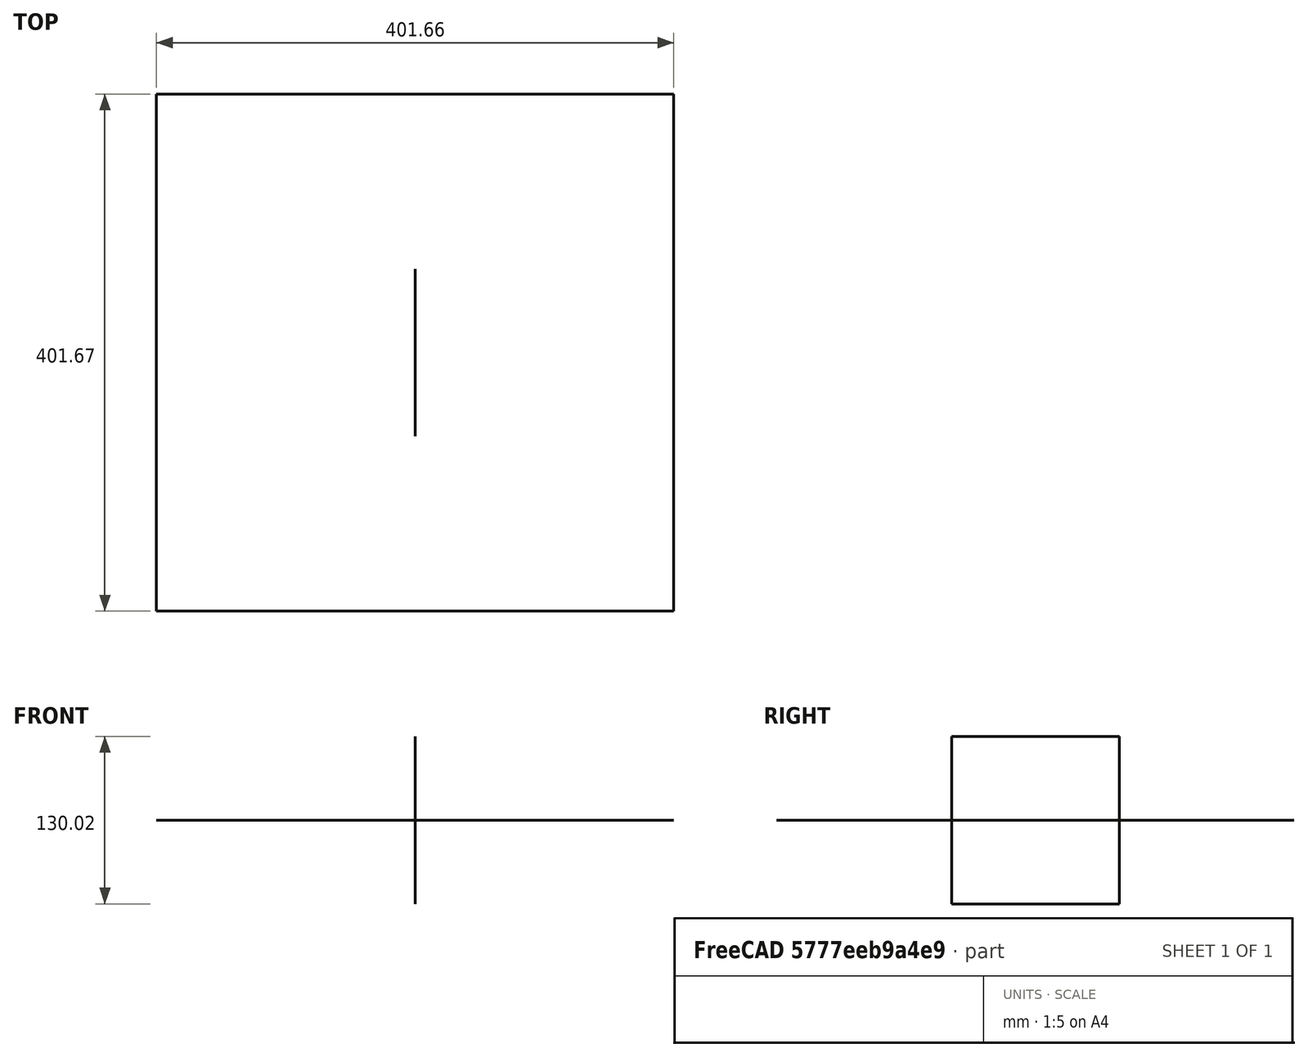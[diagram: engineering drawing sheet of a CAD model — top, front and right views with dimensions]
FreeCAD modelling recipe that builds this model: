
FCSTD DOCUMENT  (FreeCAD 2024.409R14555 (Git shallow))
Label: ValveGear_Z7S
License: All rights reserved
LicenseURL: https://en.wikipedia.org/wiki/All_rights_reserved
objects: Part::FeaturePython×97, App::FeaturePython×84, Sketcher::SketchObject×11, PartDesign::Body×11
note: 119 computed .brp shape members not serialized (recipe doc carries the construction recipe); baked Part::Feature solids carry a one-line shape summary decoded from their .brp

FEATURE [App::FeaturePython] Constraints  # WARN: FeaturePython — macro-defined, semantics opaque (R4)
  TreeRank = 13
  _LinkVersion = 1
  _Version = 1
FEATURE [Sketcher::SketchObject] Sketch001
  ArcFitTolerance = 1e-06
  AttachmentSupport = -> [XZ_Plane001]
  ExternalBSplineMaxDegree = 5
  ExternalBSplineTolerance = 0.0001
  FullyConstrained = true
  InternalTolerance = 1e-06
  InvalidShape = false
  MakeInternals = false
  MapMode = 5
  Placement = pos=(0,0,0) rot=(1,0,0;1.5708rad)
  Support = -> [XZ_Plane001]
  TreeRank = 29
  ValidateShape = false
  sketch-geometry (5):
    g0: Circle CenterX=0 CenterY=0 CenterZ=0 NormalX=0 NormalY=0 NormalZ=1 AngleXU=0 Radius=6.5
    g1: Circle CenterX=15 CenterY=0 CenterZ=0 NormalX=0 NormalY=0 NormalZ=1 AngleXU=0 Radius=3.5
    g2: LineSegment StartX=0 StartY=0 StartZ=0 EndX=15 EndY=0 EndZ=0
    g3: Circle CenterX=9e-16 CenterY=3.4 CenterZ=0 NormalX=0 NormalY=0 NormalZ=1 AngleXU=0 Radius=11
    g4: LineSegment StartX=9e-16 StartY=3.4 StartZ=0 EndX=0 EndY=0 EndZ=0
  constraints (12):
    c: Diameter(g0) = 13
    c: Coincident(g0,g-1)
    c: PointOnObject(g1,g-1)
    c: Diameter(g1) = 7
    c: Distance(g1,g0) = 15
    c: Coincident(g2,g0)
    c: Coincident(g2,g1)
    c: Diameter(g3) = 22
    c: Coincident(g4,g3)
    c: Coincident(g4,g0)
    c: Distance(g4) = 3.4
    c: Angle(g4,g2) = 4.71239
FEATURE [PartDesign::Body] Body001
  AutoGroupSolids = false
  ClaimAllChildren = false
  ExportMode = 0
  Group = -> [Sketch001]
  InvalidShape = false
  Origin = -> Origin001
  TreeRank = 28
  ValidateShape = false
  _ExportChildren = -> [Sketch001]
  _GroupVersion = 1
FEATURE [App::FeaturePython] Constraints001  # WARN: FeaturePython — macro-defined, semantics opaque (R4)
  TreeRank = 31
  _LinkVersion = 1
  _Version = 1
FEATURE [Part::FeaturePython] Parts001  # WARN: FeaturePython — macro-defined, semantics opaque (R4)
  Group = -> [Body001]
  GroupMode = 0
  InvalidShape = false
  TreeRank = 33
  ValidateShape = false
  _LinkVersion = 1
FEATURE [Sketcher::SketchObject] Sketch002
  ArcFitTolerance = 1e-06
  AttachmentSupport = -> [XZ_Plane002]
  ExternalBSplineMaxDegree = 5
  ExternalBSplineTolerance = 0.0001
  FullyConstrained = true
  InternalTolerance = 1e-06
  InvalidShape = false
  MakeInternals = false
  MapMode = 5
  Placement = pos=(0,0,0) rot=(1,0,0;1.5708rad)
  Support = -> [XZ_Plane002]
  TreeRank = 44
  ValidateShape = false
  sketch-geometry (3):
    g0: Circle CenterX=15 CenterY=0 CenterZ=0 NormalX=0 NormalY=0 NormalZ=1 AngleXU=0 Radius=4
    g1: LineSegment StartX=15 StartY=0 StartZ=0 EndX=-75 EndY=0 EndZ=0
    g2: Circle CenterX=-75 CenterY=0 CenterZ=0 NormalX=0 NormalY=0 NormalZ=1 AngleXU=0 Radius=3
  constraints (8):
    c: PointOnObject(g0,g-1)
    c: Distance(g-1,g0) = 15
    c: Diameter(g0) = 8
    c: Coincident(g1,g0)
    c: PointOnObject(g1,g-1)
    c: Distance(g1) = 90
    c: Coincident(g2,g1)
    c: Diameter(g2) = 6
FEATURE [PartDesign::Body] Body002
  AutoGroupSolids = false
  ClaimAllChildren = false
  ExportMode = 0
  Group = -> [Sketch002]
  InvalidShape = false
  Origin = -> Origin002
  TreeRank = 43
  ValidateShape = false
  _ExportChildren = -> [Sketch002]
  _GroupVersion = 1
FEATURE [App::FeaturePython] Constraints002  # WARN: FeaturePython — macro-defined, semantics opaque (R4)
  TreeRank = 46
  _LinkVersion = 1
  _Version = 1
FEATURE [Part::FeaturePython] Parts002  # WARN: FeaturePython — macro-defined, semantics opaque (R4)
  Group = -> [Body002]
  GroupMode = 0
  InvalidShape = false
  TreeRank = 48
  ValidateShape = false
  _LinkVersion = 1
FEATURE [Sketcher::SketchObject] Sketch003
  ArcFitTolerance = 1e-06
  AttachmentSupport = -> [XZ_Plane003]
  ExternalBSplineMaxDegree = 5
  ExternalBSplineTolerance = 0.0001
  FullyConstrained = false
  InternalTolerance = 1e-06
  InvalidShape = false
  MakeInternals = false
  MapMode = 5
  Placement = pos=(0,0,0) rot=(1,0,0;1.5708rad)
  Support = -> [XZ_Plane003]
  TreeRank = 68
  ValidateShape = false
  sketch-geometry (8):
    g0: Circle CenterX=-77.8195 CenterY=0 CenterZ=0 NormalX=0 NormalY=0 NormalZ=1 AngleXU=0 Radius=2
    g1: LineSegment StartX=-77.8195 StartY=0 StartZ=0 EndX=-133.569 EndY=0 EndZ=0
    g2: LineSegment StartX=-133.569 StartY=0 StartZ=0 EndX=-133.569 EndY=11 EndZ=0
    g3: LineSegment StartX=-133.569 StartY=11 StartZ=0 EndX=-143.069 EndY=11 EndZ=0
    g4: LineSegment StartX=-143.069 StartY=11 StartZ=0 EndX=-143.069 EndY=-11 EndZ=0
    g5: LineSegment StartX=-143.069 StartY=-11 StartZ=0 EndX=-133.569 EndY=-11 EndZ=0
    g6: LineSegment StartX=-133.569 StartY=-11 StartZ=0 EndX=-133.569 EndY=0 EndZ=0
    g7: GeomPoint [constr] X=-138.319 Y=0 Z=0
  constraints (20):
    c: PointOnObject(g0,g-1)
    c: Diameter(g0) = 4
    c: Coincident(g1,g0)
    c: Horizontal(g1)
    c: Distance(g1) = 55.75
    c: Coincident(g2,g1)
    c: Vertical(g2)
    c: Coincident(g3,g2)
    c: Horizontal(g3)
    c: Coincident(g4,g3)
    c: Vertical(g4)
    c: Coincident(g5,g4)
    c: Horizontal(g5)
    c: Coincident(g6,g5)
    c: Coincident(g6,g1)
    c: Distance(g4) = 22
    c: Symmetric(g2,g5,g1)
    c: Distance(g5) = 9.5
    c: PointOnObject(g7,g-1)
    c: Distance(g7,g1) = 4.75
FEATURE [PartDesign::Body] Body003
  AutoGroupSolids = false
  ClaimAllChildren = false
  ExportMode = 0
  Group = -> [Sketch003]
  InvalidShape = false
  Origin = -> Origin003
  TreeRank = 67
  ValidateShape = false
  _ExportChildren = -> [Sketch003]
  _GroupVersion = 1
FEATURE [App::FeaturePython] Constraints004  # WARN: FeaturePython — macro-defined, semantics opaque (R4)
  TreeRank = 70
  _LinkVersion = 1
  _Version = 1
FEATURE [Part::FeaturePython] Parts004  # WARN: FeaturePython — macro-defined, semantics opaque (R4)
  Group = -> [Body003]
  GroupMode = 0
  InvalidShape = false
  TreeRank = 72
  ValidateShape = false
  _LinkVersion = 1
FEATURE [Sketcher::SketchObject] Sketch004
  ArcFitTolerance = 1e-06
  AttachmentSupport = -> [XZ_Plane004]
  ExternalBSplineMaxDegree = 5
  ExternalBSplineTolerance = 0.0001
  FullyConstrained = false
  InternalTolerance = 1e-06
  InvalidShape = false
  MakeInternals = false
  MapMode = 5
  Placement = pos=(0,0,0) rot=(1,0,0;1.5708rad)
  Support = -> [XZ_Plane004]
  TreeRank = 136
  ValidateShape = false
  sketch-geometry (4):
    g0: LineSegment StartX=-73.0178 StartY=31.2839 StartZ=0 EndX=-54 EndY=-9.5 EndZ=0
    g1: Circle CenterX=-73.0178 CenterY=31.2839 CenterZ=0 NormalX=0 NormalY=0 NormalZ=1 AngleXU=0 Radius=45
    g2: LineSegment StartX=-54 StartY=-9.5 StartZ=0 EndX=-29 EndY=-9.5 EndZ=0
    g3: Circle CenterX=-54 CenterY=-9.5 CenterZ=0 NormalX=0 NormalY=0 NormalZ=1 AngleXU=0 Radius=1.13037
  constraints (10):
    c: Distance(g0) = 45
    c: Coincident(g1,g0)
    c: PointOnObject(g0,g1)
    c: Coincident(g2,g0)
    c: Horizontal(g2)
    c: Angle(g2,g0) = 2.00713  'Cutoff CTRL'
    c: Distance(g2) = 25
    c: DistanceX(g-2,g0) = -54
    c: DistanceY(g-1,g0) = -9.5
    c: Coincident(g3,g0)
FEATURE [PartDesign::Body] Body004
  AutoGroupSolids = false
  ClaimAllChildren = false
  ExportMode = 0
  Group = -> [Sketch004]
  InvalidShape = false
  Origin = -> Origin004
  TreeRank = 135
  ValidateShape = false
  _ExportChildren = -> [Sketch004]
  _GroupVersion = 1
FEATURE [App::FeaturePython] Constraints005  # WARN: FeaturePython — macro-defined, semantics opaque (R4)
  TreeRank = 138
  _LinkVersion = 1
  _Version = 1
FEATURE [Part::FeaturePython] Parts005  # WARN: FeaturePython — macro-defined, semantics opaque (R4)
  Group = -> [Body004]
  GroupMode = 0
  InvalidShape = false
  TreeRank = 140
  ValidateShape = false
  _LinkVersion = 1
FEATURE [Sketcher::SketchObject] Sketch005
  ArcFitTolerance = 1e-06
  AttachmentSupport = -> [XZ_Plane005]
  ExternalBSplineMaxDegree = 5
  ExternalBSplineTolerance = 0.0001
  FullyConstrained = false
  InternalTolerance = 1e-06
  InvalidShape = false
  MakeInternals = false
  MapMode = 5
  Placement = pos=(0,0,0) rot=(1,0,0;1.5708rad)
  Support = -> [XZ_Plane005]
  TreeRank = 152
  ValidateShape = false
  sketch-geometry (6):
    g0: LineSegment StartX=-16.5858 StartY=-34.3042 StartZ=0 EndX=-71.3858 EndY=-34.3042 EndZ=0
    g1: LineSegment StartX=-71.3858 StartY=-34.3042 StartZ=0 EndX=-91.3858 EndY=-34.3042 EndZ=0
    g2: LineSegment StartX=-71.3858 StartY=-34.3042 StartZ=0 EndX=-71.3858 EndY=-35.8042 EndZ=0
    g3: Circle CenterX=-16.5858 CenterY=-34.3042 CenterZ=0 NormalX=0 NormalY=0 NormalZ=1 AngleXU=0 Radius=11.25
    g4: Circle CenterX=-71.3858 CenterY=-35.8042 CenterZ=0 NormalX=0 NormalY=0 NormalZ=1 AngleXU=0 Radius=1
    g5: Circle CenterX=-91.3858 CenterY=-34.3042 CenterZ=0 NormalX=0 NormalY=0 NormalZ=1 AngleXU=0 Radius=1
  constraints (14):
    c: Horizontal(g0)
    c: Distance(g0) = 54.8
    c: Coincident(g1,g0)
    c: Horizontal(g1)
    c: Distance(g1) = 20
    c: Coincident(g2,g0)
    c: Vertical(g2)
    c: Distance(g2) = 1.5
    c: Coincident(g3,g0)
    c: Diameter(g3) = 22.5
    c: Coincident(g4,g2)
    c: Coincident(g5,g1)
    c: Diameter(g4) = 2
    c: Diameter(g5) = 2
FEATURE [PartDesign::Body] Body005
  AutoGroupSolids = false
  ClaimAllChildren = false
  ExportMode = 0
  Group = -> [Sketch005]
  InvalidShape = false
  Origin = -> Origin005
  TreeRank = 151
  ValidateShape = false
  _ExportChildren = -> [Sketch005]
  _GroupVersion = 1
FEATURE [App::FeaturePython] Constraints006  # WARN: FeaturePython — macro-defined, semantics opaque (R4)
  TreeRank = 154
  _LinkVersion = 1
  _Version = 1
FEATURE [Part::FeaturePython] Parts006  # WARN: FeaturePython — macro-defined, semantics opaque (R4)
  Group = -> [Body005]
  GroupMode = 0
  InvalidShape = false
  TreeRank = 156
  ValidateShape = false
  _LinkVersion = 1
FEATURE [Sketcher::SketchObject] Sketch006
  ArcFitTolerance = 1e-06
  AttachmentSupport = -> [XZ_Plane006]
  ExternalBSplineMaxDegree = 5
  ExternalBSplineTolerance = 0.0001
  FullyConstrained = false
  InternalTolerance = 1e-06
  InvalidShape = false
  MakeInternals = false
  MapMode = 5
  Placement = pos=(0,0,0) rot=(1,0,0;1.5708rad)
  Support = -> [XZ_Plane006]
  TreeRank = 195
  ValidateShape = false
  sketch-geometry (3):
    g0: LineSegment StartX=-79.4771 StartY=11.8151 StartZ=0 EndX=-79.4771 EndY=-10.4849 EndZ=0
    g1: Circle CenterX=-79.4771 CenterY=11.8151 CenterZ=0 NormalX=0 NormalY=0 NormalZ=1 AngleXU=0 Radius=2
    g2: Circle CenterX=-79.4771 CenterY=-10.4849 CenterZ=0 NormalX=0 NormalY=0 NormalZ=1 AngleXU=0 Radius=2
  constraints (6):
    c: Vertical(g0)
    c: Coincident(g1,g0)
    c: Coincident(g2,g0)
    c: Diameter(g1) = 4
    c: Equal(g1,g2)
    c: Distance(g0,g0) = 22.3
FEATURE [PartDesign::Body] Body006
  AutoGroupSolids = false
  ClaimAllChildren = false
  ExportMode = 0
  Group = -> [Sketch006]
  InvalidShape = false
  Origin = -> Origin006
  TreeRank = 194
  ValidateShape = false
  _ExportChildren = -> [Sketch006]
  _GroupVersion = 1
FEATURE [App::FeaturePython] Constraints007  # WARN: FeaturePython — macro-defined, semantics opaque (R4)
  TreeRank = 197
  _LinkVersion = 1
  _Version = 1
FEATURE [Part::FeaturePython] Parts007  # WARN: FeaturePython — macro-defined, semantics opaque (R4)
  Group = -> [Body006]
  GroupMode = 0
  InvalidShape = false
  TreeRank = 199
  ValidateShape = false
  _LinkVersion = 1
FEATURE [Sketcher::SketchObject] Sketch007
  ArcFitTolerance = 1e-06
  AttachmentSupport = -> [XZ_Plane007]
  ExternalBSplineMaxDegree = 5
  ExternalBSplineTolerance = 0.0001
  FullyConstrained = false
  InternalTolerance = 1e-06
  InvalidShape = false
  MakeInternals = false
  MapMode = 5
  Placement = pos=(0,0,0) rot=(1,0,0;1.5708rad)
  Support = -> [XZ_Plane007]
  TreeRank = 212
  ValidateShape = false
  sketch-geometry (5):
    g0: LineSegment StartX=-86.9461 StartY=28.8972 StartZ=0 EndX=-85.47 EndY=20.5263 EndZ=0
    g1: LineSegment StartX=-85.47 StartY=20.5263 StartZ=0 EndX=-76.97 EndY=20.5263 EndZ=0
    g2: Circle CenterX=-85.47 CenterY=20.5263 CenterZ=0 NormalX=0 NormalY=0 NormalZ=1 AngleXU=0 Radius=2
    g3: Circle CenterX=-76.97 CenterY=20.5263 CenterZ=0 NormalX=0 NormalY=0 NormalZ=1 AngleXU=0 Radius=1.5
    g4: Circle CenterX=-86.9461 CenterY=28.8972 CenterZ=0 NormalX=0 NormalY=0 NormalZ=1 AngleXU=0 Radius=1.5
  constraints (11):
    c: Coincident(g1,g0)
    c: Horizontal(g1)
    c: Distance(g0,g1) = 8.5
    c: Equal(g1,g0)
    c: Angle(g1,g0) = 1.74533
    c: Coincident(g2,g0)
    c: Coincident(g3,g1)
    c: Coincident(g4,g0)
    c: Diameter(g3) = 3
    c: Equal(g3,g4)
    c: Diameter(g2) = 4
FEATURE [PartDesign::Body] Body007
  AutoGroupSolids = false
  ClaimAllChildren = false
  ExportMode = 0
  Group = -> [Sketch007]
  InvalidShape = false
  Origin = -> Origin007
  TreeRank = 211
  ValidateShape = false
  _ExportChildren = -> [Sketch007]
  _GroupVersion = 1
FEATURE [App::FeaturePython] Constraints008  # WARN: FeaturePython — macro-defined, semantics opaque (R4)
  TreeRank = 214
  _LinkVersion = 1
  _Version = 1
FEATURE [Part::FeaturePython] Parts008  # WARN: FeaturePython — macro-defined, semantics opaque (R4)
  Group = -> [Body007]
  GroupMode = 0
  InvalidShape = false
  TreeRank = 216
  ValidateShape = false
  _LinkVersion = 1
FEATURE [Sketcher::SketchObject] Sketch008
  ArcFitTolerance = 1e-06
  AttachmentSupport = -> [XZ_Plane008]
  ExternalBSplineMaxDegree = 5
  ExternalBSplineTolerance = 0.0001
  FullyConstrained = false
  InternalTolerance = 1e-06
  InvalidShape = false
  MakeInternals = false
  MapMode = 5
  Placement = pos=(0,0,0) rot=(1,0,0;1.5708rad)
  Support = -> [XZ_Plane008]
  TreeRank = 246
  ValidateShape = false
  sketch-geometry (3):
    g0: LineSegment StartX=-86.6169 StartY=29.8279 StartZ=0 EndX=-98.6169 EndY=29.8279 EndZ=0
    g1: Circle CenterX=-86.6169 CenterY=29.8279 CenterZ=0 NormalX=0 NormalY=0 NormalZ=1 AngleXU=0 Radius=2
    g2: Circle CenterX=-98.6169 CenterY=29.8279 CenterZ=0 NormalX=0 NormalY=0 NormalZ=1 AngleXU=0 Radius=2
  constraints (6):
    c: Horizontal(g0)
    c: Distance(g0) = 12
    c: Coincident(g1,g0)
    c: Coincident(g2,g0)
    c: Diameter(g1) = 4
    c: Equal(g2,g1)
FEATURE [PartDesign::Body] Body008
  AutoGroupSolids = false
  ClaimAllChildren = false
  ExportMode = 0
  Group = -> [Sketch008]
  InvalidShape = false
  Origin = -> Origin008
  TreeRank = 245
  ValidateShape = false
  _ExportChildren = -> [Sketch008]
  _GroupVersion = 1
FEATURE [App::FeaturePython] Constraints009  # WARN: FeaturePython — macro-defined, semantics opaque (R4)
  TreeRank = 248
  _LinkVersion = 1
  _Version = 1
FEATURE [Part::FeaturePython] Parts009  # WARN: FeaturePython — macro-defined, semantics opaque (R4)
  Group = -> [Body008]
  GroupMode = 0
  InvalidShape = false
  TreeRank = 250
  ValidateShape = false
  _LinkVersion = 1
FEATURE [Sketcher::SketchObject] Sketch009
  ArcFitTolerance = 1e-06
  AttachmentSupport = -> [XZ_Plane009]
  ExternalBSplineMaxDegree = 5
  ExternalBSplineTolerance = 0.0001
  FullyConstrained = false
  InternalTolerance = 1e-06
  InvalidShape = false
  MakeInternals = false
  MapMode = 5
  Placement = pos=(0,0,0) rot=(1,0,0;1.5708rad)
  Support = -> [XZ_Plane009]
  TreeRank = 268
  ValidateShape = false
  sketch-geometry (13):
    g0: LineSegment StartX=-96.3044 StartY=29.3618 StartZ=0 EndX=-148.604 EndY=29.3618 EndZ=0
    g1: LineSegment StartX=-139.404 StartY=33.1118 StartZ=0 EndX=-139.404 EndY=25.6118 EndZ=0
    g2: LineSegment StartX=-139.404 StartY=33.1118 StartZ=0 EndX=-141.704 EndY=33.1118 EndZ=0
    g3: LineSegment StartX=-141.704 StartY=33.1118 StartZ=0 EndX=-141.704 EndY=25.6118 EndZ=0
    g4: LineSegment StartX=-141.704 StartY=25.6118 StartZ=0 EndX=-139.404 EndY=25.6118 EndZ=0
    g5: LineSegment StartX=-157.804 StartY=25.6118 StartZ=0 EndX=-157.804 EndY=33.1118 EndZ=0
    g6: LineSegment StartX=-157.804 StartY=33.1118 StartZ=0 EndX=-155.504 EndY=33.1118 EndZ=0
    g7: LineSegment StartX=-155.504 StartY=33.1118 StartZ=0 EndX=-155.504 EndY=25.6118 EndZ=0
    g8: LineSegment StartX=-155.504 StartY=25.6118 StartZ=0 EndX=-157.804 EndY=25.6118 EndZ=0
    g9: GeomPoint [constr] X=-156.654 Y=29.3618 Z=0
    g10: LineSegment StartX=-155.504 StartY=30.6118 StartZ=0 EndX=-141.704 EndY=30.6118 EndZ=0
    g11: LineSegment StartX=-155.504 StartY=28.1118 StartZ=0 EndX=-141.704 EndY=28.1118 EndZ=0
    g12: Circle CenterX=-96.3044 CenterY=29.3618 CenterZ=0 NormalX=0 NormalY=0 NormalZ=1 AngleXU=0 Radius=1.5
  constraints (35):
    c: Horizontal(g0)
    c: Distance(g0) = 52.3
    c: Distance(g1) = 7.5
    c: Symmetric(g1,g1,g0)
    c: Coincident(g2,g1)
    c: Horizontal(g2)
    c: Coincident(g3,g2)
    c: Vertical(g3)
    c: Coincident(g4,g3)
    c: Coincident(g4,g1)
    c: Horizontal(g4)
    c: Distance(g4) = 2.3
    c: Coincident(g5,g6)
    c: Coincident(g6,g7)
    c: Coincident(g7,g8)
    c: Coincident(g8,g5)
    c: Horizontal(g6)
    c: Horizontal(g8)
    c: Vertical(g5)
    c: Vertical(g7)
    c: Symmetric(g6,g5,g9)
    c: Horizontal(g9,g0)
    c: Equal(g6,g2)
    c: Equal(g5,g3)
    c: Distance(g5,g1) = 18.4
    c: Distance(g0,g1) = 9.2
    c: PointOnObject(g10,g7)
    c: PointOnObject(g10,g3)
    c: Horizontal(g10)
    c: PointOnObject(g11,g7)
    c: Horizontal(g11)
    c: Symmetric(g10,g11,g0)
    c: Distance(g10,g11) = 2.5
    c: Coincident(g12,g0)
    c: Diameter(g12) = 3
FEATURE [PartDesign::Body] Body009
  AutoGroupSolids = false
  ClaimAllChildren = false
  ExportMode = 0
  Group = -> [Sketch009]
  InvalidShape = false
  Origin = -> Origin009
  TreeRank = 267
  ValidateShape = false
  _ExportChildren = -> [Sketch009]
  _GroupVersion = 1
FEATURE [App::FeaturePython] Constraints010  # WARN: FeaturePython — macro-defined, semantics opaque (R4)
  TreeRank = 270
  _LinkVersion = 1
  _Version = 1
FEATURE [Part::FeaturePython] Parts010  # WARN: FeaturePython — macro-defined, semantics opaque (R4)
  Group = -> [Body009]
  GroupMode = 0
  InvalidShape = false
  TreeRank = 272
  ValidateShape = false
  _LinkVersion = 1
FEATURE [Sketcher::SketchObject] Sketch
  ArcFitTolerance = 1e-06
  AttachmentSupport = -> [XZ_Plane]
  ExternalBSplineMaxDegree = 5
  ExternalBSplineTolerance = 0.0001
  FullyConstrained = false
  InternalTolerance = 1e-06
  InvalidShape = false
  MakeInternals = false
  MapMode = 5
  Placement = pos=(0,0,0) rot=(1,0,0;1.5708rad)
  Support = -> [XZ_Plane]
  TreeRank = 315
  ValidateShape = false
  sketch-geometry (23):
    g0: LineSegment StartX=-180 StartY=63 StartZ=0 EndX=120 EndY=63 EndZ=0
    g1: LineSegment StartX=120 StartY=63 StartZ=0 EndX=120 EndY=-63 EndZ=0
    g2: LineSegment StartX=120 StartY=-63 StartZ=0 EndX=-180 EndY=-63 EndZ=0
    g3: LineSegment StartX=-180 StartY=-63 StartZ=0 EndX=-180 EndY=63 EndZ=0
    g4: Circle CenterX=0 CenterY=0 CenterZ=0 NormalX=0 NormalY=0 NormalZ=1 AngleXU=0 Radius=6.5
    g5: LineSegment StartX=0 StartY=0 StartZ=0 EndX=-180 EndY=0 EndZ=0
    g6: Circle CenterX=-54 CenterY=-9.5 CenterZ=0 NormalX=0 NormalY=0 NormalZ=1 AngleXU=0 Radius=1.5
    g7: Circle CenterX=-84 CenterY=11 CenterZ=0 NormalX=0 NormalY=0 NormalZ=1 AngleXU=0 Radius=1.27714
    g8: LineSegment StartX=-189.468 StartY=19 StartZ=0 EndX=0 EndY=19 EndZ=0
    g9: LineSegment StartX=-189.468 StartY=19 StartZ=0 EndX=-198.831 EndY=26.4354 EndZ=0
    g10: LineSegment StartX=-198.831 StartY=26.4354 StartZ=0 EndX=-198.831 EndY=11.5646 EndZ=0
    g11: LineSegment StartX=-198.831 StartY=11.5646 StartZ=0 EndX=-189.468 EndY=19 EndZ=0
    g12: LineSegment StartX=-180 StartY=0 StartZ=0 EndX=-192.162 EndY=6.36433 EndZ=0
    g13: LineSegment StartX=-192.162 StartY=6.36433 StartZ=0 EndX=-192.162 EndY=-6.36433 EndZ=0
    g14: LineSegment StartX=-192.162 StartY=-6.36433 StartZ=0 EndX=-180 EndY=0 EndZ=0
    g15: Circle CenterX=-150 CenterY=19 CenterZ=0 NormalX=0 NormalY=0 NormalZ=1 AngleXU=0 Radius=0.005
    g16: LineSegment StartX=0 StartY=0 StartZ=0 EndX=30 EndY=0 EndZ=0
    g17: LineSegment StartX=30 StartY=0 StartZ=0 EndX=34.0566 EndY=3.40069 EndZ=0
    g18: LineSegment StartX=34.0566 StartY=3.40069 StartZ=0 EndX=34.0566 EndY=-2.89461 EndZ=0
    g19: LineSegment StartX=34.0566 StartY=-2.89461 StartZ=0 EndX=30 EndY=-4e-16 EndZ=0
    g20: Circle CenterX=-150 CenterY=19 CenterZ=0 NormalX=0 NormalY=0 NormalZ=1 AngleXU=0 Radius=3.91179
    g21: LineSegment StartX=-150 StartY=63 StartZ=0 EndX=-150 EndY=-63 EndZ=0
    g22: LineSegment StartX=0 StartY=63 StartZ=0 EndX=0 EndY=-63 EndZ=0
  constraints (53):
    c: Coincident(g0,g1)
    c: Coincident(g1,g2)
    c: Coincident(g2,g3)
    c: Coincident(g3,g0)
    c: Horizontal(g0)
    c: Horizontal(g2)
    c: Vertical(g3)
    c: Distance(g1) = 126
    c: Symmetric(g0,g1,g-1)
    c: Distance(g-1,g3) = 180
    c: Coincident(g4,g-1)
    c: Diameter(g4) = 13
    c: Coincident(g5,g4)
    c: PointOnObject(g5,g3)
    c: Horizontal(g5)
    c: Diameter(g6) = 3
    c: Distance(g6,g5) = 9.5
    c: DistanceX(g-2,g6) = -54
    c: DistanceX(g7,g6) = 30
    c: DistanceY(g4,g7) = 11
    c: Horizontal(g8)
    c: Coincident(g9,g8)
    c: Coincident(g11,g10)
    c: Coincident(g11,g8)
    c: Coincident(g10,g9)
    c: DistanceY(g4,g8) = 19
    c: Coincident(g12,g5)
    c: Coincident(g13,g12)
    c: Coincident(g14,g13)
    c: Coincident(g14,g5)
    c: Symmetric(g13,g12,g5)
    c: Symmetric(g10,g9,g8)
    c: Diameter(g15) = 0.01
    c: DistanceX(g-2,g15) = -150
    c: Distance(g15,g5) = 19
    c: Coincident(g16,g4)
    c: PointOnObject(g16,g-1)
    c: Coincident(g17,g16)
    c: Coincident(g18,g17)
    c: Vertical(g18)
    c: Coincident(g19,g18)
    c: Coincident(g19,g16)
    c: Distance(g4,g16) = 30  'Dead Centre'
    c: Coincident(g20,g15)
    c: PointOnObject(g21,g0)
    c: PointOnObject(g21,g2)
    c: Vertical(g21)
    c: Distance(g4,g21) = 150
    c: PointOnObject(g22,g0)
    c: PointOnObject(g22,g2)
    c: Vertical(g22)
    c: Vertical(g22,g4)
    c: Vertical(g8,g4)
FEATURE [PartDesign::Body] Body
  AutoGroupSolids = false
  ClaimAllChildren = false
  ExportMode = 0
  Group = -> [Sketch]
  InvalidShape = false
  Origin = -> Origin
  TreeRank = 10
  ValidateShape = false
  _ExportChildren = -> [Sketch]
  _GroupVersion = 1
FEATURE [Part::FeaturePython] Parts  # WARN: FeaturePython — macro-defined, semantics opaque (R4)
  Group = -> [Body]
  GroupMode = 0
  InvalidShape = false
  TreeRank = 15
  ValidateShape = false
  _LinkVersion = 1
FEATURE [Sketcher::SketchObject] Sketch010
  ArcFitTolerance = 1e-06
  AttachmentSupport = -> [XZ_Plane010]
  ExternalBSplineMaxDegree = 5
  ExternalBSplineTolerance = 0.0001
  FullyConstrained = false
  InternalTolerance = 1e-06
  InvalidShape = false
  MakeInternals = false
  MapMode = 5
  Placement = pos=(0,0,0) rot=(1,0,0;1.5708rad)
  Support = -> [XZ_Plane010]
  TreeRank = 337
  ValidateShape = false
  sketch-geometry (15):
    g0: LineSegment StartX=-128 StartY=-12.0827 StartZ=0 EndX=-150 EndY=-12.0827 EndZ=0
    g1: LineSegment StartX=-150 StartY=-12.0827 StartZ=0 EndX=-172 EndY=-12.0827 EndZ=0
    g2: LineSegment StartX=-172 StartY=-12.0827 StartZ=0 EndX=-172 EndY=14.9774 EndZ=0
    g3: LineSegment StartX=-158 StartY=14.9774 StartZ=0 EndX=-150 EndY=14.9774 EndZ=0
    g4: LineSegment StartX=-150 StartY=14.9774 StartZ=0 EndX=-142 EndY=14.9774 EndZ=0
    g5: LineSegment StartX=-159.5 StartY=14.9774 StartZ=0 EndX=-172 EndY=14.9774 EndZ=0
    g6: LineSegment StartX=-128 StartY=-12.0827 StartZ=0 EndX=-128 EndY=14.9774 EndZ=0
    g7: LineSegment StartX=-128 StartY=14.9774 StartZ=0 EndX=-140.5 EndY=14.9774 EndZ=0
    g8: LineSegment StartX=-164.568 StartY=11.4567 StartZ=0 EndX=-150 EndY=11.4567 EndZ=0
    g9: LineSegment StartX=-150 StartY=11.4567 StartZ=0 EndX=-135.432 EndY=11.4567 EndZ=0
    g10: LineSegment StartX=-158 StartY=14.9774 StartZ=0 EndX=-164.568 EndY=11.4567 EndZ=0
    g11: LineSegment StartX=-142 StartY=14.9774 StartZ=0 EndX=-135.432 EndY=11.4567 EndZ=0
    g12: LineSegment StartX=-159.5 StartY=14.9774 StartZ=0 EndX=-172 EndY=11.6516 EndZ=0
    g13: LineSegment StartX=-140.5 StartY=14.9774 StartZ=0 EndX=-128 EndY=11.6516 EndZ=0
    g14: GeomPoint [constr] X=0 Y=0 Z=0
  constraints (36):
    c: Horizontal(g0)
    c: DistanceX(g-2,g0) = -150
    c: Coincident(g1,g0)
    c: Symmetric(g1,g0,g0)
    c: Distance(g0,g0) = 22
    c: Coincident(g2,g1)
    c: Vertical(g2)
    c: Horizontal(g3)
    c: Coincident(g4,g3)
    c: Symmetric(g4,g3,g3)
    c: Vertical(g3,g0)
    c: Distance(g3,g4) = 8
    c: Horizontal(g5)
    c: Horizontal(g5,g3)
    c: Distance(g5,g3) = 1.5
    c: Coincident(g2,g5)
    c: Coincident(g6,g0)
    c: Vertical(g6)
    c: Equal(g6,g2)
    c: Coincident(g7,g6)
    c: Horizontal(g7)
    c: Equal(g7,g5)
    c: Horizontal(g8)
    c: Vertical(g8,g3)
    c: Coincident(g9,g8)
    c: Symmetric(g9,g8,g8)
    c: Coincident(g10,g3)
    c: Coincident(g10,g8)
    c: Coincident(g11,g4)
    c: Coincident(g11,g9)
    c: Coincident(g12,g5)
    c: PointOnObject(g12,g2)
    c: Coincident(g13,g7)
    c: PointOnObject(g13,g6)
    c: Equal(g12,g13)
    c: Coincident(g14,g-1)
FEATURE [PartDesign::Body] Body010
  AutoGroupSolids = false
  ClaimAllChildren = false
  ExportMode = 0
  Group = -> [Sketch010]
  InvalidShape = false
  Origin = -> Origin010
  TreeRank = 336
  ValidateShape = false
  _ExportChildren = -> [Sketch010]
  _GroupVersion = 1
FEATURE [Part::FeaturePython] Assembly  # WARN: FeaturePython — macro-defined, semantics opaque (R4)
  AutoRelax = true
  BuildShape = 0
  Freeze = false
  Group = -> [Constraints,Elements,Parts]
  InvalidShape = false
  Placement = pos=(-4.26503e-11,0.00833303,-5.51265e-07) rot=(-1,0,0;0.000132rad)
  TreeRank = 12
  ValidateShape = false
  Verbose = false
  _LinkVersion = 1
  _SolverType = 1
  _Version = 1
FEATURE [App::FeaturePython] Elements  # WARN: FeaturePython — macro-defined, semantics opaque (R4)
  Group = -> [_Element,Element007,Element008,Element009,Element015,Element021,Element026,Element028,Element029,Element031,Element033,Element035,Element036]
  TreeRank = 14
  _LinkVersion = 1
FEATURE [Part::FeaturePython] _Element  # link proxy (typed FeaturePython)
  Detach = false
  InvalidShape = false
  LinkTransform = true
  LinkedObject = -> Body [Sketch.Edge5]
  TreeRank = 18
  ValidateShape = false
  _LinkVersion = 1
  _Parent = -> Elements
FEATURE [Part::FeaturePython] Assembly001  # WARN: FeaturePython — macro-defined, semantics opaque (R4)
  AutoRelax = true
  BuildShape = 0
  Freeze = false
  Group = -> [Constraints001,Elements001,Parts001]
  InvalidShape = false
  Placement = pos=(-4.27174e-11,0.00833336,-5.51309e-07) rot=(1,0,0;6.28305rad)
  TreeRank = 30
  ValidateShape = false
  Verbose = false
  _LinkVersion = 1
  _SolverType = 1
  _Version = 1
FEATURE [App::FeaturePython] Elements001  # WARN: FeaturePython — macro-defined, semantics opaque (R4)
  Group = -> [Element,Element001,Element002,Element027]
  TreeRank = 32
  _LinkVersion = 1
FEATURE [Part::FeaturePython] Assembly002  # WARN: FeaturePython — macro-defined, semantics opaque (R4)
  AutoRelax = true
  BuildShape = 0
  Freeze = false
  Group = -> [Constraints002,Elements002,Parts002]
  InvalidShape = false
  Placement = pos=(1.58905e-10,0.00833336,-5.51309e-07) rot=(-1,0,0;0.000132rad)
  TreeRank = 45
  ValidateShape = false
  Verbose = false
  _LinkVersion = 1
  _SolverType = 1
  _Version = 1
FEATURE [App::FeaturePython] Elements002  # WARN: FeaturePython — macro-defined, semantics opaque (R4)
  Group = -> [Element003,Element004]
  TreeRank = 47
  _LinkVersion = 1
FEATURE [Part::FeaturePython] Assembly003  # WARN: FeaturePython — macro-defined, semantics opaque (R4)
  AutoRelax = true
  BuildShape = 0
  Freeze = false
  Group = -> [Constraints003,Elements003,Parts003]
  InvalidShape = false
  TreeRank = 49
  ValidateShape = false
  Verbose = false
  _LinkVersion = 1
  _SolverType = 1
  _Version = 1
FEATURE [App::FeaturePython] Constraints003  # WARN: FeaturePython — macro-defined, semantics opaque (R4)
  Group = -> [Constraint,Constraint001,Constraint002,Constraint003,Constraint004,Constraint005,Constraint007,Constraint008,Constraint009,Constraint010,Constraint011,Constraint012,Constraint013,Constraint014,Constraint015,Constraint016,Constraint018,Constraint019,Constraint020,Constraint021,Constraint022]
  TreeRank = 50
  _LinkVersion = 1
  _Version = 1
FEATURE [App::FeaturePython] Elements003  # WARN: FeaturePython — macro-defined, semantics opaque (R4)
  Group = -> [_Element001,_Element002,_Element003,_Element004,_Element005,_Element006,_Element007,_Element008,_Element009,_Element011,_Element012,_Element013,_Element014,_Element015,_Element016,_Element017,_Element018,_Element019,_Element020,_Element021,_Element022,_Element023,_Element024,_Element025,_Element026,_Element028,_Element029,_Element030,_Element031,_Element032,_Element033,_Element034,_Element035,+4 more]
  TreeRank = 51
  _LinkVersion = 1
FEATURE [Part::FeaturePython] Parts003  # WARN: FeaturePython — macro-defined, semantics opaque (R4)
  Group = -> [Assembly002,Assembly001,Assembly,Assembly004,Assembly005,Assembly006,Assembly007,Assembly008,Assembly009,Assembly010]
  GroupMode = 0
  InvalidShape = false
  TreeRank = 52
  ValidateShape = false
  _LinkVersion = 1
FEATURE [Part::FeaturePython] Element  # link proxy (typed FeaturePython)
  Detach = false
  InvalidShape = false
  LinkTransform = true
  LinkedObject = -> Body001 [Sketch001.Edge1]
  TreeRank = 53
  ValidateShape = false
  _LinkVersion = 1
  _Parent = -> Elements001
FEATURE [Part::FeaturePython] Element001  # link proxy (typed FeaturePython)
  Detach = false
  InvalidShape = false
  LinkTransform = true
  LinkedObject = -> Body001 [Sketch001.Edge5]
  TreeRank = 54
  ValidateShape = false
  _LinkVersion = 1
  _Parent = -> Elements001
FEATURE [Part::FeaturePython] Element002  # link proxy (typed FeaturePython)
  Detach = false
  InvalidShape = false
  LinkTransform = true
  LinkedObject = -> Body001 [Sketch001.Edge2]
  TreeRank = 55
  ValidateShape = false
  _LinkVersion = 1
  _Parent = -> Elements001
FEATURE [Part::FeaturePython] Element003  # link proxy (typed FeaturePython)
  Detach = false
  InvalidShape = false
  LinkTransform = true
  LinkedObject = -> Body002 [Sketch002.Edge1]
  TreeRank = 56
  ValidateShape = false
  _LinkVersion = 1
  _Parent = -> Elements002
FEATURE [Part::FeaturePython] Element004  # link proxy (typed FeaturePython)
  Detach = false
  InvalidShape = false
  LinkTransform = true
  LinkedObject = -> Body002 [Sketch002.Edge3]
  TreeRank = 57
  ValidateShape = false
  _LinkVersion = 1
  _Parent = -> Elements002
FEATURE [Part::FeaturePython] Assembly004  # WARN: FeaturePython — macro-defined, semantics opaque (R4)
  AutoRelax = true
  BuildShape = 0
  Freeze = false
  Group = -> [Constraints004,Elements004,Parts004]
  InvalidShape = false
  Placement = pos=(2.81946,0.00833091,-0.0185483) rot=(-0.485257,0.874371,-5.8e-05;0.000273rad)
  TreeRank = 69
  ValidateShape = false
  Verbose = false
  _LinkVersion = 1
  _SolverType = 1
  _Version = 1
FEATURE [App::FeaturePython] Elements004  # WARN: FeaturePython — macro-defined, semantics opaque (R4)
  Group = -> [Element005,Element006,Element030]
  TreeRank = 71
  _LinkVersion = 1
FEATURE [Part::FeaturePython] Element005  # link proxy (typed FeaturePython)
  Detach = false
  InvalidShape = false
  LinkTransform = true
  LinkedObject = -> Body003 [Sketch003.Edge1]
  TreeRank = 73
  ValidateShape = false
  _LinkVersion = 1
  _Parent = -> Elements004
FEATURE [Part::FeaturePython] Element006  # link proxy (typed FeaturePython)
  Detach = false
  InvalidShape = false
  LinkTransform = true
  LinkedObject = -> Body003 [Sketch003.Edge2]
  TreeRank = 74
  ValidateShape = false
  _LinkVersion = 1
  _Parent = -> Elements004
FEATURE [App::FeaturePython] Constraint  label="Locked"  # WARN: FeaturePython — macro-defined, semantics opaque (R4)
  Disabled = false
  Group = -> [ElementLink]
  TreeRank = 75
  _ConstraintType = 0
  _LinkVersion = 1
  _Parent = -> Constraints003
FEATURE [App::FeaturePython] ElementLink  label="_Element001"  # link proxy (typed FeaturePython)
  LinkTransform = true
  LinkedObject = -> _Element001
  TreeRank = 76
  _LinkVersion = 1
  _Parent = -> Constraint
FEATURE [Part::FeaturePython] Element007  # link proxy (typed FeaturePython)
  Detach = false
  InvalidShape = false
  LinkTransform = true
  LinkedObject = -> Body [Sketch.Edge3]
  TreeRank = 77
  ValidateShape = false
  _LinkVersion = 1
  _Parent = -> Elements
FEATURE [Part::FeaturePython] _Element001  # link proxy (typed FeaturePython)
  Detach = false
  InvalidShape = false
  LinkTransform = true
  LinkedObject = -> Assembly [1.$Element007.]
  TreeRank = 78
  ValidateShape = false
  _LinkVersion = 1
  _Parent = -> Elements003
FEATURE [Part::FeaturePython] _Element002  # link proxy (typed FeaturePython)
  Detach = false
  InvalidShape = false
  LinkTransform = true
  LinkedObject = -> Assembly [1.$_Element.]
  TreeRank = 81
  ValidateShape = false
  _LinkVersion = 1
  _Parent = -> Elements003
FEATURE [Part::FeaturePython] _Element003  # link proxy (typed FeaturePython)
  Detach = false
  InvalidShape = false
  LinkTransform = true
  LinkedObject = -> Assembly001 [1.$Element.]
  TreeRank = 83
  ValidateShape = false
  _LinkVersion = 1
  _Parent = -> Elements003
FEATURE [App::FeaturePython] Constraint001  label="PlaneCoincident.Driver"  # WARN: FeaturePython — macro-defined, semantics opaque (R4)
  Angle = 360
  AnglePitch = 0
  AngleRoll = 0
  Cascade = false
  Disabled = false
  Group = -> [ElementLink001,ElementLink002]
  LockAngle = true
  Multiply = false
  OffsetX = 0
  OffsetY = 0
  TreeRank = 84
  _ConstraintType = 35
  _LinkVersion = 1
  _Parent = -> Constraints003
FEATURE [App::FeaturePython] ElementLink001  label="_Element002"  # link proxy (typed FeaturePython)
  LinkTransform = true
  LinkedObject = -> _Element002
  TreeRank = 85
  _LinkVersion = 1
  _Parent = -> Constraint001
FEATURE [App::FeaturePython] ElementLink002  label="_Element003"  # link proxy (typed FeaturePython)
  LinkTransform = true
  LinkedObject = -> _Element003
  TreeRank = 86
  _LinkVersion = 1
  _Parent = -> Constraint001
FEATURE [App::FeaturePython] Constraint002  label="PlaneCoincident001"  # WARN: FeaturePython — macro-defined, semantics opaque (R4)
  Angle = 0
  AnglePitch = 0
  AngleRoll = 0
  Cascade = false
  Disabled = false
  Group = -> [ElementLink003,ElementLink004]
  LockAngle = false
  Multiply = false
  OffsetX = 0
  OffsetY = 0
  TreeRank = 87
  _ConstraintType = 35
  _LinkVersion = 1
  _Parent = -> Constraints003
FEATURE [App::FeaturePython] ElementLink003  label="_Element004"  # link proxy (typed FeaturePython)
  LinkTransform = true
  LinkedObject = -> _Element004
  TreeRank = 88
  _LinkVersion = 1
  _Parent = -> Constraint002
FEATURE [Part::FeaturePython] _Element004  # link proxy (typed FeaturePython)
  Detach = false
  InvalidShape = false
  LinkTransform = true
  LinkedObject = -> Assembly001 [1.$Element002.]
  TreeRank = 89
  ValidateShape = false
  _LinkVersion = 1
  _Parent = -> Elements003
FEATURE [App::FeaturePython] ElementLink004  label="_Element005"  # link proxy (typed FeaturePython)
  LinkTransform = true
  LinkedObject = -> _Element005
  TreeRank = 90
  _LinkVersion = 1
  _Parent = -> Constraint002
FEATURE [Part::FeaturePython] _Element005  # link proxy (typed FeaturePython)
  Detach = false
  InvalidShape = false
  LinkTransform = true
  LinkedObject = -> Assembly002 [1.$Element003.]
  TreeRank = 91
  ValidateShape = false
  _LinkVersion = 1
  _Parent = -> Elements003
FEATURE [App::FeaturePython] Constraint003  label="PlaneCoincident002"  # WARN: FeaturePython — macro-defined, semantics opaque (R4)
  Angle = 0
  AnglePitch = 0
  AngleRoll = 0
  Cascade = false
  Disabled = false
  Group = -> [ElementLink005,ElementLink006]
  LockAngle = false
  Multiply = false
  OffsetX = 0
  OffsetY = 0
  TreeRank = 92
  _ConstraintType = 35
  _LinkVersion = 1
  _Parent = -> Constraints003
FEATURE [App::FeaturePython] ElementLink005  label="_Element006"  # link proxy (typed FeaturePython)
  LinkTransform = true
  LinkedObject = -> _Element006
  TreeRank = 93
  _LinkVersion = 1
  _Parent = -> Constraint003
FEATURE [Part::FeaturePython] _Element006  # link proxy (typed FeaturePython)
  Detach = false
  InvalidShape = false
  LinkTransform = true
  LinkedObject = -> Assembly002 [1.$Element004.]
  TreeRank = 94
  ValidateShape = false
  _LinkVersion = 1
  _Parent = -> Elements003
FEATURE [App::FeaturePython] ElementLink006  label="_Element007"  # link proxy (typed FeaturePython)
  LinkTransform = true
  LinkedObject = -> _Element007
  TreeRank = 95
  _LinkVersion = 1
  _Parent = -> Constraint003
FEATURE [Part::FeaturePython] _Element007  # link proxy (typed FeaturePython)
  Detach = false
  InvalidShape = false
  LinkTransform = true
  LinkedObject = -> Assembly004 [1.$Element005.]
  TreeRank = 96
  ValidateShape = false
  _LinkVersion = 1
  _Parent = -> Elements003
FEATURE [Part::FeaturePython] Element008  # link proxy (typed FeaturePython)
  Detach = false
  InvalidShape = false
  LinkTransform = true
  LinkedObject = -> Body [Sketch.edge6]
  TreeRank = 97
  ValidateShape = false
  _LinkVersion = 1
  _Parent = -> Elements
FEATURE [Part::FeaturePython] _Element008  # link proxy (typed FeaturePython)
  Detach = false
  InvalidShape = false
  LinkTransform = true
  LinkedObject = -> Assembly [1.$Element008.]
  TreeRank = 100
  ValidateShape = false
  _LinkVersion = 1
  _Parent = -> Elements003
FEATURE [Part::FeaturePython] _Element009  # link proxy (typed FeaturePython)
  Detach = false
  InvalidShape = false
  LinkTransform = true
  LinkedObject = -> Assembly004 [1.$Element006.]
  TreeRank = 102
  ValidateShape = false
  _LinkVersion = 1
  _Parent = -> Elements003
FEATURE [Part::FeaturePython] Element009  # link proxy (typed FeaturePython)
  Detach = false
  InvalidShape = false
  LinkTransform = true
  LinkedObject = -> Body [Sketch.Edge14]
  TreeRank = 114
  ValidateShape = false
  _LinkVersion = 1
  _Parent = -> Elements
FEATURE [Part::FeaturePython] _Element011  # link proxy (typed FeaturePython)
  Detach = false
  InvalidShape = false
  LinkTransform = true
  LinkedObject = -> Assembly [1.$Element009.]
  TreeRank = 125
  ValidateShape = false
  _LinkVersion = 1
  _Parent = -> Elements003
FEATURE [Part::FeaturePython] Assembly005  # WARN: FeaturePython — macro-defined, semantics opaque (R4)
  AutoRelax = true
  BuildShape = 0
  Freeze = false
  Group = -> [Constraints005,Elements005,Parts005]
  InvalidShape = false
  Placement = pos=(-4.28482e-11,0.00833303,-5.51265e-07) rot=(-1,0,0;0.000132rad)
  TreeRank = 137
  ValidateShape = false
  Verbose = false
  _LinkVersion = 1
  _SolverType = 1
  _Version = 1
FEATURE [App::FeaturePython] Elements005  # WARN: FeaturePython — macro-defined, semantics opaque (R4)
  Group = -> [Element010,Element014]
  TreeRank = 139
  _LinkVersion = 1
FEATURE [Part::FeaturePython] Element010  # link proxy (typed FeaturePython)
  Detach = false
  InvalidShape = false
  LinkTransform = true
  LinkedObject = -> Body004 [Sketch004.Edge3]
  TreeRank = 141
  ValidateShape = false
  _LinkVersion = 1
  _Parent = -> Elements005
FEATURE [Part::FeaturePython] Assembly006  # WARN: FeaturePython — macro-defined, semantics opaque (R4)
  AutoRelax = true
  BuildShape = 0
  Freeze = false
  Group = -> [Constraints006,Elements006,Parts006]
  InvalidShape = false
  Placement = pos=(9.27701,0.0136716,40.3568) rot=(-0.000645,-1,6.6e-05;0.204413rad)
  TreeRank = 153
  ValidateShape = false
  Verbose = false
  _LinkVersion = 1
  _SolverType = 1
  _Version = 1
FEATURE [App::FeaturePython] Elements006  # WARN: FeaturePython — macro-defined, semantics opaque (R4)
  Group = -> [Element011,Element012,Element013]
  TreeRank = 155
  _LinkVersion = 1
FEATURE [Part::FeaturePython] Element011  # link proxy (typed FeaturePython)
  Detach = false
  InvalidShape = false
  LinkTransform = true
  LinkedObject = -> Body005 [Sketch005.Edge4]
  TreeRank = 157
  ValidateShape = false
  _LinkVersion = 1
  _Parent = -> Elements006
FEATURE [Part::FeaturePython] Element012  # link proxy (typed FeaturePython)
  Detach = false
  InvalidShape = false
  LinkTransform = true
  LinkedObject = -> Body005 [Sketch005.Edge5]
  TreeRank = 158
  ValidateShape = false
  _LinkVersion = 1
  _Parent = -> Elements006
FEATURE [Part::FeaturePython] Element013  # link proxy (typed FeaturePython)
  Detach = false
  InvalidShape = false
  LinkTransform = true
  LinkedObject = -> Body005 [Sketch005.Edge6]
  TreeRank = 159
  ValidateShape = false
  _LinkVersion = 1
  _Parent = -> Elements006
FEATURE [App::FeaturePython] Constraint005  label="PlaneCoincident003"  # WARN: FeaturePython — macro-defined, semantics opaque (R4)
  Angle = 0
  AnglePitch = 0
  AngleRoll = 0
  Cascade = false
  Disabled = false
  Group = -> [ElementLink009,ElementLink010]
  LockAngle = false
  Multiply = false
  OffsetX = 0
  OffsetY = 0
  TreeRank = 160
  _ConstraintType = 35
  _LinkVersion = 1
  _Parent = -> Constraints003
FEATURE [App::FeaturePython] ElementLink009  label="_Element012"  # link proxy (typed FeaturePython)
  LinkTransform = true
  LinkedObject = -> _Element012
  TreeRank = 161
  _LinkVersion = 1
  _Parent = -> Constraint005
FEATURE [Part::FeaturePython] _Element012  # link proxy (typed FeaturePython)
  Detach = false
  InvalidShape = false
  LinkTransform = true
  LinkedObject = -> Assembly001 [1.$Element001.]
  TreeRank = 162
  ValidateShape = false
  _LinkVersion = 1
  _Parent = -> Elements003
FEATURE [App::FeaturePython] ElementLink010  label="_Element013"  # link proxy (typed FeaturePython)
  LinkTransform = true
  LinkedObject = -> _Element013
  TreeRank = 163
  _LinkVersion = 1
  _Parent = -> Constraint005
FEATURE [Part::FeaturePython] _Element013  # link proxy (typed FeaturePython)
  Detach = false
  InvalidShape = false
  LinkTransform = true
  LinkedObject = -> Assembly006 [1.$Element011.]
  TreeRank = 164
  ValidateShape = false
  _LinkVersion = 1
  _Parent = -> Elements003
FEATURE [Part::FeaturePython] _Element014  # link proxy (typed FeaturePython)
  Detach = false
  InvalidShape = false
  LinkTransform = true
  LinkedObject = -> Assembly006 [1.$Element012.]
  TreeRank = 167
  ValidateShape = false
  _LinkVersion = 1
  _Parent = -> Elements003
FEATURE [Part::FeaturePython] _Element015  # link proxy (typed FeaturePython)
  Detach = false
  InvalidShape = false
  LinkTransform = true
  LinkedObject = -> Assembly005 [1.$Element010.]
  TreeRank = 169
  ValidateShape = false
  _LinkVersion = 1
  _Parent = -> Elements003
FEATURE [Part::FeaturePython] Element014  # link proxy (typed FeaturePython)
  Detach = false
  InvalidShape = false
  LinkTransform = true
  LinkedObject = -> Body004 [Sketch004.Edge4]
  TreeRank = 170
  ValidateShape = false
  _LinkVersion = 1
  _Parent = -> Elements005
FEATURE [App::FeaturePython] Constraint007  label="PlaneCoincident004"  # WARN: FeaturePython — macro-defined, semantics opaque (R4)
  Angle = 0
  AnglePitch = 0
  AngleRoll = 0
  Cascade = false
  Disabled = false
  Group = -> [ElementLink013,ElementLink014]
  LockAngle = true
  Multiply = false
  OffsetX = 0
  OffsetY = 0
  TreeRank = 171
  _ConstraintType = 35
  _LinkVersion = 1
  _Parent = -> Constraints003
FEATURE [App::FeaturePython] ElementLink013  label="_Element011"  # link proxy (typed FeaturePython)
  LinkTransform = true
  LinkedObject = -> _Element011
  TreeRank = 172
  _LinkVersion = 1
  _Parent = -> Constraint007
FEATURE [App::FeaturePython] ElementLink014  label="_Element016"  # link proxy (typed FeaturePython)
  LinkTransform = true
  LinkedObject = -> _Element016
  TreeRank = 173
  _LinkVersion = 1
  _Parent = -> Constraint007
FEATURE [Part::FeaturePython] _Element016  # link proxy (typed FeaturePython)
  Detach = false
  InvalidShape = false
  LinkTransform = true
  LinkedObject = -> Assembly005 [1.$Element014.]
  TreeRank = 174
  ValidateShape = false
  _LinkVersion = 1
  _Parent = -> Elements003
FEATURE [App::FeaturePython] Constraint008  label="PointsOnCircle001"  # WARN: FeaturePython — macro-defined, semantics opaque (R4)
  Disabled = false
  Group = -> [ElementLink015,ElementLink016]
  TreeRank = 175
  _ConstraintType = 26
  _LinkVersion = 1
  _Parent = -> Constraints003
FEATURE [App::FeaturePython] ElementLink015  label="_Element014"  # link proxy (typed FeaturePython)
  LinkTransform = true
  LinkedObject = -> _Element014
  TreeRank = 176
  _LinkVersion = 1
  _Parent = -> Constraint008
FEATURE [App::FeaturePython] ElementLink016  label="_Element015"  # link proxy (typed FeaturePython)
  LinkTransform = true
  LinkedObject = -> _Element015
  TreeRank = 177
  _LinkVersion = 1
  _Parent = -> Constraint008
FEATURE [App::FeaturePython] Constraint009  label="PointOnLine"  # WARN: FeaturePython — macro-defined, semantics opaque (R4)
  Disabled = false
  Group = -> [ElementLink017,ElementLink018]
  TreeRank = 178
  _ConstraintType = 4
  _LinkVersion = 1
  _Parent = -> Constraints003
FEATURE [App::FeaturePython] ElementLink017  label="_Element007"  # link proxy (typed FeaturePython)
  LinkTransform = true
  LinkedObject = -> _Element007
  TreeRank = 179
  _LinkVersion = 1
  _Parent = -> Constraint009
FEATURE [App::FeaturePython] ElementLink018  label="_Element008"  # link proxy (typed FeaturePython)
  LinkTransform = true
  LinkedObject = -> _Element008
  TreeRank = 180
  _LinkVersion = 1
  _Parent = -> Constraint009
FEATURE [App::FeaturePython] ElementLink007  label="_Element008"  # link proxy (typed FeaturePython)
  LinkTransform = true
  LinkedObject = -> _Element008
  TreeRank = 181
  _LinkVersion = 1
  _Parent = -> Constraint004
FEATURE [App::FeaturePython] ElementLink008  label="_Element009"  # link proxy (typed FeaturePython)
  LinkTransform = true
  LinkedObject = -> _Element009
  TreeRank = 182
  _LinkVersion = 1
  _Parent = -> Constraint004
FEATURE [App::FeaturePython] Constraint004  label="MultiParallel"  # WARN: FeaturePython — macro-defined, semantics opaque (R4)
  Angle = 0
  AnglePitch = 0
  AngleRoll = 0
  Disabled = true
  Group = -> [ElementLink007,ElementLink008]
  LockAngle = false
  TreeRank = 183
  _ConstraintType = 291
  _LinkVersion = 1
  _Parent = -> Constraints003
FEATURE [Part::FeaturePython] Element015  # link proxy (typed FeaturePython)
  Detach = false
  InvalidShape = false
  LinkTransform = true
  LinkedObject = -> Body [Sketch.edge8]
  TreeRank = 184
  ValidateShape = false
  _LinkVersion = 1
  _Parent = -> Elements
FEATURE [Part::FeaturePython] Assembly007  # WARN: FeaturePython — macro-defined, semantics opaque (R4)
  AutoRelax = true
  BuildShape = 0
  Freeze = false
  Group = -> [Constraints007,Elements007,Parts007]
  InvalidShape = false
  Placement = pos=(4.74708,0.00922847,6.76695) rot=(-0.001291,-0.999999,6.6e-05;0.102356rad)
  TreeRank = 196
  ValidateShape = false
  Verbose = false
  _LinkVersion = 1
  _SolverType = 1
  _Version = 1
FEATURE [App::FeaturePython] Elements007  # WARN: FeaturePython — macro-defined, semantics opaque (R4)
  Group = -> [Element016,Element017,Element034]
  TreeRank = 198
  _LinkVersion = 1
FEATURE [Part::FeaturePython] Element016  # link proxy (typed FeaturePython)
  Detach = false
  InvalidShape = false
  LinkTransform = true
  LinkedObject = -> Body006 [Sketch006.Edge3]
  TreeRank = 200
  ValidateShape = false
  _LinkVersion = 1
  _Parent = -> Elements007
FEATURE [Part::FeaturePython] Element017  # link proxy (typed FeaturePython)
  Detach = false
  InvalidShape = false
  LinkTransform = true
  LinkedObject = -> Body006 [Sketch006.Edge2]
  TreeRank = 201
  ValidateShape = false
  _LinkVersion = 1
  _Parent = -> Elements007
FEATURE [Part::FeaturePython] Assembly008  # WARN: FeaturePython — macro-defined, semantics opaque (R4)
  AutoRelax = true
  BuildShape = 0
  Freeze = false
  Group = -> [Constraints008,Elements008,Parts008]
  InvalidShape = false
  Placement = pos=(-0.193868,0.00628124,-15.514) rot=(-0.00187,0.999998,-6.6e-05;0.070715rad)
  TreeRank = 213
  ValidateShape = false
  Verbose = false
  _LinkVersion = 1
  _SolverType = 1
  _Version = 1
FEATURE [App::FeaturePython] Elements008  # WARN: FeaturePython — macro-defined, semantics opaque (R4)
  Group = -> [Element018,Element019,Element020]
  TreeRank = 215
  _LinkVersion = 1
FEATURE [Part::FeaturePython] Element018  # link proxy (typed FeaturePython)
  Detach = false
  InvalidShape = false
  LinkTransform = true
  LinkedObject = -> Body007 [Sketch007.Edge3]
  TreeRank = 217
  ValidateShape = false
  _LinkVersion = 1
  _Parent = -> Elements008
FEATURE [Part::FeaturePython] Element019  # link proxy (typed FeaturePython)
  Detach = false
  InvalidShape = false
  LinkTransform = true
  LinkedObject = -> Body007 [Sketch007.Edge4]
  TreeRank = 218
  ValidateShape = false
  _LinkVersion = 1
  _Parent = -> Elements008
FEATURE [Part::FeaturePython] Element020  # link proxy (typed FeaturePython)
  Detach = false
  InvalidShape = false
  LinkTransform = true
  LinkedObject = -> Body007 [Sketch007.Edge5]
  TreeRank = 219
  ValidateShape = false
  _LinkVersion = 1
  _Parent = -> Elements008
FEATURE [App::FeaturePython] Constraint010  label="PlaneCoincident"  # WARN: FeaturePython — macro-defined, semantics opaque (R4)
  Angle = 0
  AnglePitch = 0
  AngleRoll = 0
  Cascade = false
  Disabled = false
  Group = -> [ElementLink019,ElementLink020]
  LockAngle = false
  Multiply = false
  OffsetX = 0
  OffsetY = 0
  TreeRank = 220
  _ConstraintType = 35
  _LinkVersion = 1
  _Parent = -> Constraints003
FEATURE [App::FeaturePython] ElementLink019  label="_Element017"  # link proxy (typed FeaturePython)
  LinkTransform = true
  LinkedObject = -> _Element017
  TreeRank = 221
  _LinkVersion = 1
  _Parent = -> Constraint010
FEATURE [Part::FeaturePython] _Element017  # link proxy (typed FeaturePython)
  Detach = false
  InvalidShape = false
  LinkTransform = true
  LinkedObject = -> Assembly007 [1.$Element016.]
  TreeRank = 222
  ValidateShape = false
  _LinkVersion = 1
  _Parent = -> Elements003
FEATURE [App::FeaturePython] ElementLink020  label="_Element018"  # link proxy (typed FeaturePython)
  LinkTransform = true
  LinkedObject = -> _Element018
  TreeRank = 223
  _LinkVersion = 1
  _Parent = -> Constraint010
FEATURE [Part::FeaturePython] _Element018  # link proxy (typed FeaturePython)
  Detach = false
  InvalidShape = false
  LinkTransform = true
  LinkedObject = -> Assembly006 [1.$Element013.]
  TreeRank = 224
  ValidateShape = false
  _LinkVersion = 1
  _Parent = -> Elements003
FEATURE [App::FeaturePython] Constraint011  label="PlaneCoincident005"  # WARN: FeaturePython — macro-defined, semantics opaque (R4)
  Angle = 0
  AnglePitch = 0
  AngleRoll = 0
  Cascade = false
  Disabled = false
  Group = -> [ElementLink021,ElementLink022]
  LockAngle = false
  Multiply = false
  OffsetX = 0
  OffsetY = 0
  TreeRank = 225
  _ConstraintType = 35
  _LinkVersion = 1
  _Parent = -> Constraints003
FEATURE [App::FeaturePython] ElementLink021  label="_Element019"  # link proxy (typed FeaturePython)
  LinkTransform = true
  LinkedObject = -> _Element019
  TreeRank = 226
  _LinkVersion = 1
  _Parent = -> Constraint011
FEATURE [Part::FeaturePython] _Element019  # link proxy (typed FeaturePython)
  Detach = false
  InvalidShape = false
  LinkTransform = true
  LinkedObject = -> Assembly008 [1.$Element018.]
  TreeRank = 227
  ValidateShape = false
  _LinkVersion = 1
  _Parent = -> Elements003
FEATURE [App::FeaturePython] ElementLink022  label="_Element020"  # link proxy (typed FeaturePython)
  LinkTransform = true
  LinkedObject = -> _Element020
  TreeRank = 228
  _LinkVersion = 1
  _Parent = -> Constraint011
FEATURE [Part::FeaturePython] _Element020  # link proxy (typed FeaturePython)
  Detach = false
  InvalidShape = false
  LinkTransform = true
  LinkedObject = -> Assembly [1.$Element015.]
  TreeRank = 229
  ValidateShape = false
  _LinkVersion = 1
  _Parent = -> Elements003
FEATURE [App::FeaturePython] Constraint012  label="PlaneCoincident006"  # WARN: FeaturePython — macro-defined, semantics opaque (R4)
  Angle = 0
  AnglePitch = 0
  AngleRoll = 0
  Cascade = false
  Disabled = false
  Group = -> [ElementLink023,ElementLink024]
  LockAngle = false
  Multiply = false
  OffsetX = 0
  OffsetY = 0
  TreeRank = 230
  _ConstraintType = 35
  _LinkVersion = 1
  _Parent = -> Constraints003
FEATURE [App::FeaturePython] ElementLink023  label="_Element021"  # link proxy (typed FeaturePython)
  LinkTransform = true
  LinkedObject = -> _Element021
  TreeRank = 231
  _LinkVersion = 1
  _Parent = -> Constraint012
FEATURE [Part::FeaturePython] _Element021  # link proxy (typed FeaturePython)
  Detach = false
  InvalidShape = false
  LinkTransform = true
  LinkedObject = -> Assembly008 [1.$Element019.]
  TreeRank = 232
  ValidateShape = false
  _LinkVersion = 1
  _Parent = -> Elements003
FEATURE [App::FeaturePython] ElementLink024  label="_Element022"  # link proxy (typed FeaturePython)
  LinkTransform = true
  LinkedObject = -> _Element022
  TreeRank = 233
  _LinkVersion = 1
  _Parent = -> Constraint012
FEATURE [Part::FeaturePython] _Element022  # link proxy (typed FeaturePython)
  Detach = false
  InvalidShape = false
  LinkTransform = true
  LinkedObject = -> Assembly007 [1.$Element017.]
  TreeRank = 234
  ValidateShape = false
  _LinkVersion = 1
  _Parent = -> Elements003
FEATURE [Part::FeaturePython] Element021  # link proxy (typed FeaturePython)
  Detach = false
  InvalidShape = false
  LinkTransform = true
  LinkedObject = -> Body [Sketch.Edge19]
  TreeRank = 235
  ValidateShape = false
  _LinkVersion = 1
  _Parent = -> Elements
FEATURE [Part::FeaturePython] Assembly009  # WARN: FeaturePython — macro-defined, semantics opaque (R4)
  AutoRelax = true
  BuildShape = 0
  Freeze = false
  Group = -> [Constraints009,Elements009,Parts009]
  InvalidShape = false
  Placement = pos=(2.80302,0.0073977,-7.07357) rot=(-0.003493,-0.999994,6.6e-05;0.037862rad)
  TreeRank = 247
  ValidateShape = false
  Verbose = false
  _LinkVersion = 1
  _SolverType = 1
  _Version = 1
FEATURE [App::FeaturePython] Elements009  # WARN: FeaturePython — macro-defined, semantics opaque (R4)
  Group = -> [Element022,Element023]
  TreeRank = 249
  _LinkVersion = 1
FEATURE [Part::FeaturePython] Element022  # link proxy (typed FeaturePython)
  Detach = false
  InvalidShape = false
  LinkTransform = true
  LinkedObject = -> Body008 [Sketch008.Edge3]
  TreeRank = 251
  ValidateShape = false
  _LinkVersion = 1
  _Parent = -> Elements009
FEATURE [Part::FeaturePython] Element023  # link proxy (typed FeaturePython)
  Detach = false
  InvalidShape = false
  LinkTransform = true
  LinkedObject = -> Body008 [Sketch008.Edge2]
  TreeRank = 252
  ValidateShape = false
  _LinkVersion = 1
  _Parent = -> Elements009
FEATURE [App::FeaturePython] Constraint013  label="PlaneCoincident007"  # WARN: FeaturePython — macro-defined, semantics opaque (R4)
  Angle = 0
  AnglePitch = 0
  AngleRoll = 0
  Cascade = false
  Disabled = false
  Group = -> [ElementLink025,ElementLink026]
  LockAngle = false
  Multiply = false
  OffsetX = 0
  OffsetY = 0
  TreeRank = 253
  _ConstraintType = 35
  _LinkVersion = 1
  _Parent = -> Constraints003
FEATURE [App::FeaturePython] ElementLink025  label="_Element023"  # link proxy (typed FeaturePython)
  LinkTransform = true
  LinkedObject = -> _Element023
  TreeRank = 254
  _LinkVersion = 1
  _Parent = -> Constraint013
FEATURE [Part::FeaturePython] _Element023  # link proxy (typed FeaturePython)
  Detach = false
  InvalidShape = false
  LinkTransform = true
  LinkedObject = -> Assembly009 [1.$Element023.]
  TreeRank = 255
  ValidateShape = false
  _LinkVersion = 1
  _Parent = -> Elements003
FEATURE [App::FeaturePython] ElementLink026  label="_Element024"  # link proxy (typed FeaturePython)
  LinkTransform = true
  LinkedObject = -> _Element024
  TreeRank = 256
  _LinkVersion = 1
  _Parent = -> Constraint013
FEATURE [Part::FeaturePython] _Element024  # link proxy (typed FeaturePython)
  Detach = false
  InvalidShape = false
  LinkTransform = true
  LinkedObject = -> Assembly008 [1.$Element020.]
  TreeRank = 257
  ValidateShape = false
  _LinkVersion = 1
  _Parent = -> Elements003
FEATURE [Part::FeaturePython] Assembly010  # WARN: FeaturePython — macro-defined, semantics opaque (R4)
  AutoRelax = true
  BuildShape = 0
  Freeze = false
  Group = -> [Constraints010,Elements010,Parts010]
  InvalidShape = false
  Placement = pos=(-0.567846,0.00696275,-10.3618) rot=(-1,0,0;0.000132rad)
  TreeRank = 269
  ValidateShape = false
  Verbose = false
  _LinkVersion = 1
  _SolverType = 1
  _Version = 1
FEATURE [App::FeaturePython] Elements010  # WARN: FeaturePython — macro-defined, semantics opaque (R4)
  Group = -> [Element024,Element025,Element032]
  TreeRank = 271
  _LinkVersion = 1
FEATURE [Part::FeaturePython] Element024  # link proxy (typed FeaturePython)
  Detach = false
  InvalidShape = false
  LinkTransform = true
  LinkedObject = -> Body009 [Sketch009.Edge12]
  TreeRank = 273
  ValidateShape = false
  _LinkVersion = 1
  _Parent = -> Elements010
FEATURE [App::FeaturePython] Constraint014  label="PlaneCoincident008"  # WARN: FeaturePython — macro-defined, semantics opaque (R4)
  Angle = 0
  AnglePitch = 0
  AngleRoll = 0
  Cascade = false
  Disabled = false
  Group = -> [ElementLink027,ElementLink028]
  LockAngle = false
  Multiply = false
  OffsetX = 0
  OffsetY = 0
  TreeRank = 275
  _ConstraintType = 35
  _LinkVersion = 1
  _Parent = -> Constraints003
FEATURE [App::FeaturePython] ElementLink027  label="_Element025"  # link proxy (typed FeaturePython)
  LinkTransform = true
  LinkedObject = -> _Element025
  TreeRank = 276
  _LinkVersion = 1
  _Parent = -> Constraint014
FEATURE [Part::FeaturePython] _Element025  # link proxy (typed FeaturePython)
  Detach = false
  InvalidShape = false
  LinkTransform = true
  LinkedObject = -> Assembly010 [1.$Element024.]
  TreeRank = 277
  ValidateShape = false
  _LinkVersion = 1
  _Parent = -> Elements003
FEATURE [App::FeaturePython] ElementLink028  label="_Element026"  # link proxy (typed FeaturePython)
  LinkTransform = true
  LinkedObject = -> _Element026
  TreeRank = 278
  _LinkVersion = 1
  _Parent = -> Constraint014
FEATURE [Part::FeaturePython] _Element026  # link proxy (typed FeaturePython)
  Detach = false
  InvalidShape = false
  LinkTransform = true
  LinkedObject = -> Assembly009 [1.$Element022.]
  TreeRank = 279
  ValidateShape = false
  _LinkVersion = 1
  _Parent = -> Elements003
FEATURE [Part::FeaturePython] _Element028  # link proxy (typed FeaturePython)
  Detach = false
  InvalidShape = false
  LinkTransform = true
  LinkedObject = -> Assembly [1.$Element021.]
  TreeRank = 284
  ValidateShape = false
  _LinkVersion = 1
  _Parent = -> Elements003
FEATURE [App::FeaturePython] Constraint015  label="PointOnLine001"  # WARN: FeaturePython — macro-defined, semantics opaque (R4)
  Disabled = false
  Group = -> [ElementLink029,ElementLink030]
  TreeRank = 285
  _ConstraintType = 4
  _LinkVersion = 1
  _Parent = -> Constraints003
FEATURE [App::FeaturePython] ElementLink029  label="_Element025"  # link proxy (typed FeaturePython)
  LinkTransform = true
  LinkedObject = -> _Element025
  TreeRank = 286
  _LinkVersion = 1
  _Parent = -> Constraint015
FEATURE [App::FeaturePython] ElementLink030  label="_Element028"  # link proxy (typed FeaturePython)
  LinkTransform = true
  LinkedObject = -> _Element028
  TreeRank = 287
  _LinkVersion = 1
  _Parent = -> Constraint015
FEATURE [Part::FeaturePython] Element025  # link proxy (typed FeaturePython)
  Detach = false
  InvalidShape = false
  LinkTransform = true
  LinkedObject = -> Body009 [Sketch009.Vertex2]
  TreeRank = 288
  ValidateShape = false
  _LinkVersion = 1
  _Parent = -> Elements010
FEATURE [App::FeaturePython] Constraint016  label="PointOnLine002"  # WARN: FeaturePython — macro-defined, semantics opaque (R4)
  Disabled = false
  Group = -> [ElementLink031,ElementLink032]
  TreeRank = 289
  _ConstraintType = 4
  _LinkVersion = 1
  _Parent = -> Constraints003
FEATURE [App::FeaturePython] ElementLink031  label="_Element029"  # link proxy (typed FeaturePython)
  LinkTransform = true
  LinkedObject = -> _Element029
  TreeRank = 290
  _LinkVersion = 1
  _Parent = -> Constraint016
FEATURE [Part::FeaturePython] _Element029  # link proxy (typed FeaturePython)
  Detach = false
  InvalidShape = false
  LinkTransform = true
  LinkedObject = -> Assembly010 [1.$Element025.]
  TreeRank = 291
  ValidateShape = false
  _LinkVersion = 1
  _Parent = -> Elements003
FEATURE [App::FeaturePython] ElementLink032  label="_Element028"  # link proxy (typed FeaturePython)
  LinkTransform = true
  LinkedObject = -> _Element028
  TreeRank = 292
  _LinkVersion = 1
  _Parent = -> Constraint016
FEATURE [Part::FeaturePython] Element026  # link proxy (typed FeaturePython)
  Detach = false
  InvalidShape = false
  LinkTransform = true
  LinkedObject = -> Body [Sketch.Edge20]
  TreeRank = 293
  ValidateShape = false
  _LinkVersion = 1
  _Parent = -> Elements
FEATURE [Part::FeaturePython] _Element030  # link proxy (typed FeaturePython)
  Detach = false
  InvalidShape = false
  LinkTransform = true
  LinkedObject = -> Assembly [1.$Element026.]
  TreeRank = 297
  ValidateShape = false
  _LinkVersion = 1
  _Parent = -> Elements003
FEATURE [Part::FeaturePython] Element027  # link proxy (typed FeaturePython)
  Detach = false
  InvalidShape = false
  LinkTransform = true
  LinkedObject = -> Body001 [Sketch001.Edge4]
  TreeRank = 298
  ValidateShape = false
  _LinkVersion = 1
  _Parent = -> Elements001
FEATURE [Part::FeaturePython] Element028  # link proxy (typed FeaturePython)
  Detach = false
  InvalidShape = false
  LinkTransform = true
  LinkedObject = -> Body [Sketch.Edge9]
  TreeRank = 299
  ValidateShape = false
  _LinkVersion = 1
  _Parent = -> Elements
FEATURE [App::FeaturePython] Constraint018  label="MeasureAngle"  # WARN: FeaturePython — macro-defined, semantics opaque (R4)
  Angle = 0
  Disabled = false
  Group = -> [ElementLink035,ElementLink036]
  Supplement = false
  TreeRank = 300
  _ConstraintType = 43
  _LinkVersion = 1
  _Parent = -> Constraints003
  expr: Label2 = .Angle
FEATURE [App::FeaturePython] ElementLink035  label="_Element031"  # link proxy (typed FeaturePython)
  LinkTransform = true
  LinkedObject = -> _Element031
  TreeRank = 301
  _LinkVersion = 1
  _Parent = -> Constraint018
FEATURE [Part::FeaturePython] _Element031  # link proxy (typed FeaturePython)
  Detach = false
  InvalidShape = false
  LinkTransform = true
  LinkedObject = -> Assembly001 [1.$Element027.]
  TreeRank = 302
  ValidateShape = false
  _LinkVersion = 1
  _Parent = -> Elements003
FEATURE [App::FeaturePython] ElementLink036  label="_Element032"  # link proxy (typed FeaturePython)
  LinkTransform = true
  LinkedObject = -> _Element032
  TreeRank = 303
  _LinkVersion = 1
  _Parent = -> Constraint018
FEATURE [Part::FeaturePython] _Element032  # link proxy (typed FeaturePython)
  Detach = false
  InvalidShape = false
  LinkTransform = true
  LinkedObject = -> Assembly [1.$Element028.]
  TreeRank = 304
  ValidateShape = false
  _LinkVersion = 1
  _Parent = -> Elements003
FEATURE [Part::FeaturePython] Element029  # link proxy (typed FeaturePython)
  Detach = false
  InvalidShape = false
  LinkTransform = true
  LinkedObject = -> Body [Sketch.Edge4]
  TreeRank = 305
  ValidateShape = false
  _LinkVersion = 1
  _Parent = -> Elements
FEATURE [Part::FeaturePython] Element030  # link proxy (typed FeaturePython)
  Detach = false
  InvalidShape = false
  LinkTransform = true
  LinkedObject = -> Body003 [Sketch003.vertex14]
  TreeRank = 306
  ValidateShape = false
  _LinkVersion = 1
  _Parent = -> Elements004
FEATURE [App::FeaturePython] Constraint019  label="MeasurePointLine"  # WARN: FeaturePython — macro-defined, semantics opaque (R4)
  Disabled = false
  Distance = 44.5
  Group = -> [ElementLink037,ElementLink038]
  TreeRank = 307
  _ConstraintType = 41
  _LinkVersion = 1
  _Parent = -> Constraints003
  expr: Label2 = .Distance
FEATURE [App::FeaturePython] ElementLink037  label="_Element033"  # link proxy (typed FeaturePython)
  LinkTransform = true
  LinkedObject = -> _Element033
  TreeRank = 308
  _LinkVersion = 1
  _Parent = -> Constraint019
FEATURE [Part::FeaturePython] _Element033  # link proxy (typed FeaturePython)
  Detach = false
  InvalidShape = false
  LinkTransform = true
  LinkedObject = -> Assembly004 [1.$Element030.]
  TreeRank = 309
  ValidateShape = false
  _LinkVersion = 1
  _Parent = -> Elements003
FEATURE [App::FeaturePython] ElementLink038  label="_Element034"  # link proxy (typed FeaturePython)
  LinkTransform = true
  LinkedObject = -> _Element034
  TreeRank = 310
  _LinkVersion = 1
  _Parent = -> Constraint019
FEATURE [Part::FeaturePython] _Element034  # link proxy (typed FeaturePython)
  Detach = false
  InvalidShape = false
  LinkTransform = true
  LinkedObject = -> Assembly [1.$Element029.]
  TreeRank = 311
  ValidateShape = false
  _LinkVersion = 1
  _Parent = -> Elements003
FEATURE [Part::FeaturePython] Element031  # link proxy (typed FeaturePython)
  Detach = false
  InvalidShape = false
  LinkTransform = true
  LinkedObject = -> Body [Sketch.Edge23]
  TreeRank = 316
  ValidateShape = false
  _LinkVersion = 1
  _Parent = -> Elements
FEATURE [Part::FeaturePython] Element032  # link proxy (typed FeaturePython)
  Detach = false
  InvalidShape = false
  LinkTransform = true
  LinkedObject = -> Body009 [Sketch009.Edge2]
  TreeRank = 317
  ValidateShape = false
  _LinkVersion = 1
  _Parent = -> Elements010
FEATURE [Part::FeaturePython] _Element035  # link proxy (typed FeaturePython)
  Detach = false
  InvalidShape = false
  LinkTransform = true
  LinkedObject = -> Assembly [1.$Element031.]
  TreeRank = 321
  ValidateShape = false
  _LinkVersion = 1
  _Parent = -> Elements003
FEATURE [Part::FeaturePython] Element033  # link proxy (typed FeaturePython)
  Detach = false
  InvalidShape = false
  LinkTransform = true
  LinkedObject = -> Body [Sketch.vertex15]
  TreeRank = 322
  ValidateShape = false
  _LinkVersion = 1
  _Parent = -> Elements
FEATURE [App::FeaturePython] Constraint020  label="MeasurePoints"  # WARN: FeaturePython — macro-defined, semantics opaque (R4)
  Disabled = false
  Distance = 149.172
  Group = -> [ElementLink039,ElementLink040]
  TreeRank = 323
  _ConstraintType = 40
  _LinkVersion = 1
  _Parent = -> Constraints003
  expr: Label2 = .Distance
FEATURE [App::FeaturePython] ElementLink039  label="_Element029"  # link proxy (typed FeaturePython)
  LinkTransform = true
  LinkedObject = -> _Element029
  TreeRank = 324
  _LinkVersion = 1
  _Parent = -> Constraint020
FEATURE [App::FeaturePython] ElementLink040  label="_Element036"  # link proxy (typed FeaturePython)
  LinkTransform = true
  LinkedObject = -> _Element036
  TreeRank = 325
  _LinkVersion = 1
  _Parent = -> Constraint020
FEATURE [Part::FeaturePython] _Element036  # link proxy (typed FeaturePython)
  Detach = false
  InvalidShape = false
  LinkTransform = true
  LinkedObject = -> Assembly [1.$Element033.]
  TreeRank = 326
  ValidateShape = false
  _LinkVersion = 1
  _Parent = -> Elements003
FEATURE [Part::FeaturePython] Element034  # link proxy (typed FeaturePython)
  Detach = false
  InvalidShape = false
  LinkTransform = true
  LinkedObject = -> Body006 [Sketch006.Vertex2]
  TreeRank = 340
  ValidateShape = false
  _LinkVersion = 1
  _Parent = -> Elements007
FEATURE [Part::FeaturePython] _Element037  # link proxy (typed FeaturePython)
  Detach = false
  InvalidShape = false
  LinkTransform = true
  LinkedObject = -> Assembly007 [1.$Element034.]
  TreeRank = 341
  ValidateShape = false
  _LinkVersion = 1
  _Parent = -> Elements003
FEATURE [Part::FeaturePython] Element035  label="YZ-plane@Body@"  # link proxy (typed FeaturePython)
  Detach = false
  InvalidShape = false
  LinkTransform = true
  LinkedObject = -> Body [Origin.YZ_Plane.]
  TreeRank = 343
  ValidateShape = false
  _LinkVersion = 1
  _Parent = -> Elements
FEATURE [Part::FeaturePython] _Element038  label="YZ-plane@Assembly@"  # link proxy (typed FeaturePython)
  Detach = false
  InvalidShape = false
  LinkTransform = true
  LinkedObject = -> Assembly [1.$YZ-plane@Body@.]
  TreeRank = 344
  ValidateShape = false
  _LinkVersion = 1
  _Parent = -> Elements003
FEATURE [App::FeaturePython] Constraint021  label="MeasurePointPlane"  # WARN: FeaturePython — macro-defined, semantics opaque (R4)
  Disabled = false
  Distance = -73.2427
  Group = -> [ElementLink041,ElementLink042]
  TreeRank = 345
  _ConstraintType = 42
  _LinkVersion = 1
  _Parent = -> Constraints003
  expr: Label2 = .Distance
FEATURE [App::FeaturePython] ElementLink041  label="_Element037"  # link proxy (typed FeaturePython)
  LinkTransform = true
  LinkedObject = -> _Element037
  TreeRank = 346
  _LinkVersion = 1
  _Parent = -> Constraint021
FEATURE [App::FeaturePython] ElementLink042  label="YZ-plane@Assembly@"  # link proxy (typed FeaturePython)
  LinkTransform = true
  LinkedObject = -> _Element038
  TreeRank = 347
  _LinkVersion = 1
  _Parent = -> Constraint021
FEATURE [App::FeaturePython] Constraint022  label="MeasurePointPlane001"  # WARN: FeaturePython — macro-defined, semantics opaque (R4)
  Disabled = false
  Distance = -11.7839
  Group = -> [ElementLink043,ElementLink044]
  TreeRank = 348
  _ConstraintType = 42
  _LinkVersion = 1
  _Parent = -> Constraints003
  expr: Label2 = .Distance
FEATURE [App::FeaturePython] ElementLink043  label="_Element037"  # link proxy (typed FeaturePython)
  LinkTransform = true
  LinkedObject = -> _Element037
  TreeRank = 349
  _LinkVersion = 1
  _Parent = -> Constraint022
FEATURE [App::FeaturePython] ElementLink044  label="XY-plane@Assembly@"  # link proxy (typed FeaturePython)
  LinkTransform = true
  LinkedObject = -> _Element039
  TreeRank = 350
  _LinkVersion = 1
  _Parent = -> Constraint022
FEATURE [Part::FeaturePython] Element036  label="XY-plane@Body@"  # link proxy (typed FeaturePython)
  Detach = false
  InvalidShape = false
  LinkTransform = true
  LinkedObject = -> Body [Origin.XY_Plane.]
  TreeRank = 351
  ValidateShape = false
  _LinkVersion = 1
  _Parent = -> Elements
FEATURE [Part::FeaturePython] _Element039  label="XY-plane@Assembly@"  # link proxy (typed FeaturePython)
  Detach = false
  InvalidShape = false
  LinkTransform = true
  LinkedObject = -> Assembly [1.$XY-plane@Body@.]
  TreeRank = 352
  ValidateShape = false
  _LinkVersion = 1
  _Parent = -> Elements003
